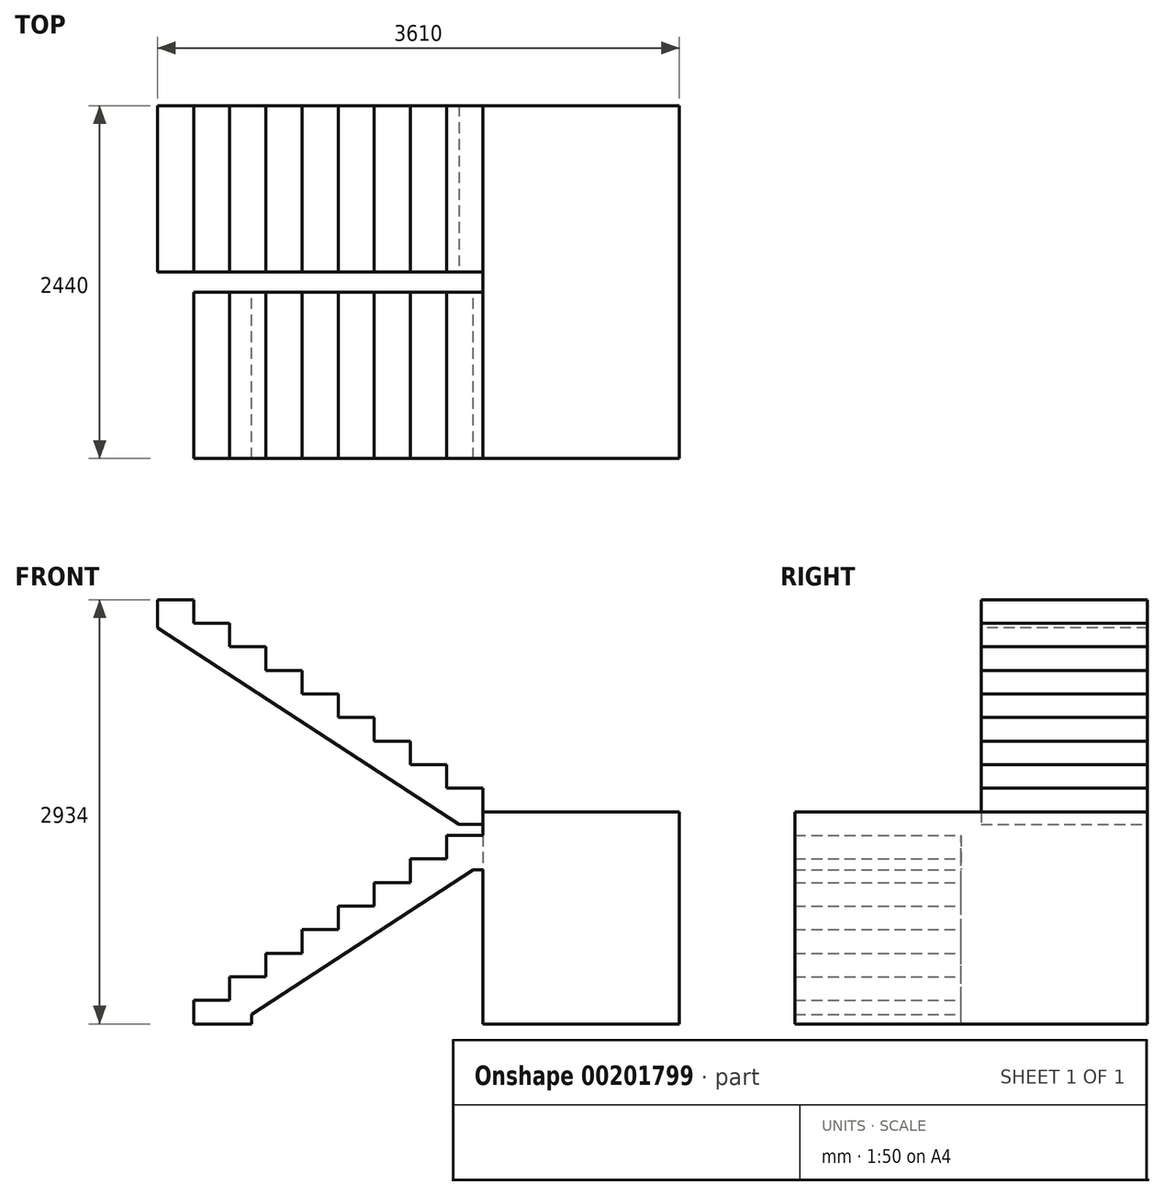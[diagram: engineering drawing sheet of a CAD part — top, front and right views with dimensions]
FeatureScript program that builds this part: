
annotation { "Feature Type Name" : "Feature", "Feature Type Description" : "" }
export const myFeature = defineFeature(function(context is Context, id is Id, definition is map)
    precondition{}
    {
        {
            var Q0;
            Q0=qCreatedBy(makeId("Front.planeOp"),FACE);
            var sketch = newSketch(context, id + "F0", { "sketchPlane" : qUnion([Q0])});
            skLineSegment(sketch, "E0", {"start": v(0, 0) * mm, "end": v(0, 163) * mm});
            skLineSegment(sketch, "E1", {"start": v(0, 163) * mm, "end": v(250, 163) * mm});
            skLineSegment(sketch, "E2", {"start": v(250, 163) * mm, "end": v(250, 326) * mm});
            skLineSegment(sketch, "E3", {"start": v(250, 326) * mm, "end": v(500, 326) * mm});
            skLineSegment(sketch, "E4", {"start": v(0, 163) * mm, "end": v(250, 326) * mm, "construction": true});
            skLineSegment(sketch, "E5", {"start": v(500, 326) * mm, "end": v(500, 489) * mm});
            skLineSegment(sketch, "E6", {"start": v(500, 489) * mm, "end": v(750, 489) * mm});
            skLineSegment(sketch, "E7", {"start": v(750, 489) * mm, "end": v(750, 652) * mm});
            skLineSegment(sketch, "E8", {"start": v(750, 652) * mm, "end": v(1000, 652) * mm});
            skLineSegment(sketch, "E9", {"start": v(1000, 652) * mm, "end": v(1000, 815) * mm});
            skLineSegment(sketch, "E10", {"start": v(1000, 815) * mm, "end": v(1250, 815) * mm});
            skLineSegment(sketch, "E11", {"start": v(1250, 815) * mm, "end": v(1250, 978) * mm});
            skLineSegment(sketch, "E12", {"start": v(1250, 978) * mm, "end": v(1500, 978) * mm});
            skLineSegment(sketch, "E13", {"start": v(1500, 978) * mm, "end": v(1500, 1141) * mm});
            skLineSegment(sketch, "E14", {"start": v(1500, 1141) * mm, "end": v(1750, 1141) * mm});
            skLineSegment(sketch, "E15", {"start": v(1750, 1141) * mm, "end": v(1750, 1304) * mm});
            skLineSegment(sketch, "E16", {"start": v(1750, 1304) * mm, "end": v(2000, 1304) * mm});
            skLineSegment(sketch, "E17", {"start": v(2000, 1304) * mm, "end": v(2000, 1467) * mm});
            skLineSegment(sketch, "E18", {"start": v(2000, 1467) * mm, "end": v(2250, 1467) * mm});
            skLineSegment(sketch, "E19", {"start": v(0, 0) * mm, "end": v(400, 0) * mm});
            skLineSegment(sketch, "E20", {"start": v(400, 0) * mm, "end": v(400, 65.67) * mm});
            skLineSegment(sketch, "E21", {"start": v(2250, 1467) * mm, "end": v(2250, 1067) * mm});
            skLineSegment(sketch, "E22.0", {"start": v(400, 65.67) * mm, "end": v(1935.79, 1067) * mm});
            skLineSegment(sketch, "E23", {"start": v(2250, 1067) * mm, "end": v(1935.79, 1067) * mm});
            skSolve(sketch);
        }
        {
            var Q0;
            Q0 = qSketchRegion(id + "F0", true);
            extrude(context, id + "F1", {"entities" : qUnion([Q0]), "depth" : 1150 * mm});
        }
        {
            var Q0;
            Q0=qCreatedBy(makeId("Front.planeOp"),FACE);
            cPlane(context, id + "F2", {"entities" : qUnion([Q0]), "cplaneType" : CPlaneType.OFFSET, "offset" : 140 * mm, "oppositeDirection" : true, "width" : 150 * mm, "height" : 150 * mm});
        }
        {
            var Q0;
            Q0=qCreatedBy(id+"F2.planeOp",FACE);
            var sketch = newSketch(context, id + "F3", { "sketchPlane" : qUnion([Q0])});
            skLineSegment(sketch, "E24.MirrorCS", {"start": v(1750, 1630) * mm, "end": v(1750, 1793) * mm});
            skLineSegment(sketch, "E25.MirrorCS", {"start": v(2000, 1467) * mm, "end": v(2000, 1630) * mm});
            skLineSegment(sketch, "E26.MirrorCS", {"start": v(500, 2608) * mm, "end": v(250, 2608) * mm});
            skLineSegment(sketch, "E27.MirrorCS", {"start": v(500, 2445) * mm, "end": v(500, 2608) * mm});
            skLineSegment(sketch, "E28.MirrorCS", {"start": v(250, 2771) * mm, "end": v(0, 2771) * mm});
            skLineSegment(sketch, "E29.MirrorCS", {"start": v(750, 2445) * mm, "end": v(500, 2445) * mm});
            skLineSegment(sketch, "E30.MirrorCS", {"start": v(750, 2282) * mm, "end": v(750, 2445) * mm});
            skLineSegment(sketch, "E31.MirrorCS", {"start": v(0, 2771) * mm, "end": v(0, 2934) * mm});
            skLineSegment(sketch, "E32.MirrorCS", {"start": v(-250, 2934) * mm, "end": v(-250, 2738.87) * mm});
            skLineSegment(sketch, "E33.MirrorCS", {"start": v(250, 2608) * mm, "end": v(250, 2771) * mm});
            skLineSegment(sketch, "E34.MirrorCS", {"start": v(0, 2934) * mm, "end": v(-250, 2934) * mm});
            skLineSegment(sketch, "E35.MirrorCS", {"start": v(1000, 2282) * mm, "end": v(750, 2282) * mm});
            skLineSegment(sketch, "E36.MirrorCS", {"start": v(1000, 2119) * mm, "end": v(1000, 2282) * mm});
            skLineSegment(sketch, "E37.MirrorCS", {"start": v(1250, 2119) * mm, "end": v(1000, 2119) * mm});
            skLineSegment(sketch, "E38.MirrorCS", {"start": v(1250, 1956) * mm, "end": v(1250, 2119) * mm});
            skLineSegment(sketch, "E39.MirrorCS", {"start": v(1500, 1956) * mm, "end": v(1250, 1956) * mm});
            skLineSegment(sketch, "E40.MirrorCS", {"start": v(1500, 1793) * mm, "end": v(1500, 1956) * mm});
            skLineSegment(sketch, "E41.MirrorCS", {"start": v(2000, 1630) * mm, "end": v(1750, 1793) * mm, "construction": true});
            skLineSegment(sketch, "E42.MirrorCS", {"start": v(1750, 1793) * mm, "end": v(1500, 1793) * mm});
            skLineSegment(sketch, "E43.MirrorCS", {"start": v(2000, 1630) * mm, "end": v(1750, 1630) * mm});
            skLineSegment(sketch, "E44.0", {"start": v(-250, 2738.87) * mm, "end": v(1836.15, 1378.7) * mm});
            skLineSegment(sketch, "E45", {"start": v(1836.15, 1378.7) * mm, "end": v(2256.1, 1378.7) * mm});
            skLineSegment(sketch, "E46", {"start": v(2256.1, 1378.7) * mm, "end": v(2256.1, 1467) * mm});
            skLineSegment(sketch, "E47", {"start": v(2256.1, 1467) * mm, "end": v(2000, 1467) * mm});
            skSolve(sketch);
        }
        {
            var Q0;
            Q0 = qSketchRegion(id + "F3", true);
            extrude(context, id + "F4", {"entities" : qUnion([Q0]), "oppositeDirection" : true, "depth" : 1150 * mm});
        }
        {
            var Q0;
            Q0=qCreatedBy(makeId("Top.planeOp"),FACE);
            var sketch = newSketch(context, id + "F5", { "sketchPlane" : qUnion([Q0])});
            skLineSegment(sketch, "E48.bottom", {"start": v(2000, -1150) * mm, "end": v(3360, -1150) * mm});
            skLineSegment(sketch, "E48.top", {"start": v(2000, 1290) * mm, "end": v(3360, 1290) * mm});
            skLineSegment(sketch, "E48.left", {"start": v(2000, -1150) * mm, "end": v(2000, 1290) * mm});
            skLineSegment(sketch, "E48.right", {"start": v(3360, -1150) * mm, "end": v(3360, 1290) * mm});
            skSolve(sketch);
        }
        {
            var Q0;
            Q0 = qSketchRegion(id + "F5", true);
            extrude(context, id + "F6", {"entities" : qUnion([Q0]), "operationType" : NewBodyOperationType.ADD, "depth" : 1467 * mm});
        }
    });
